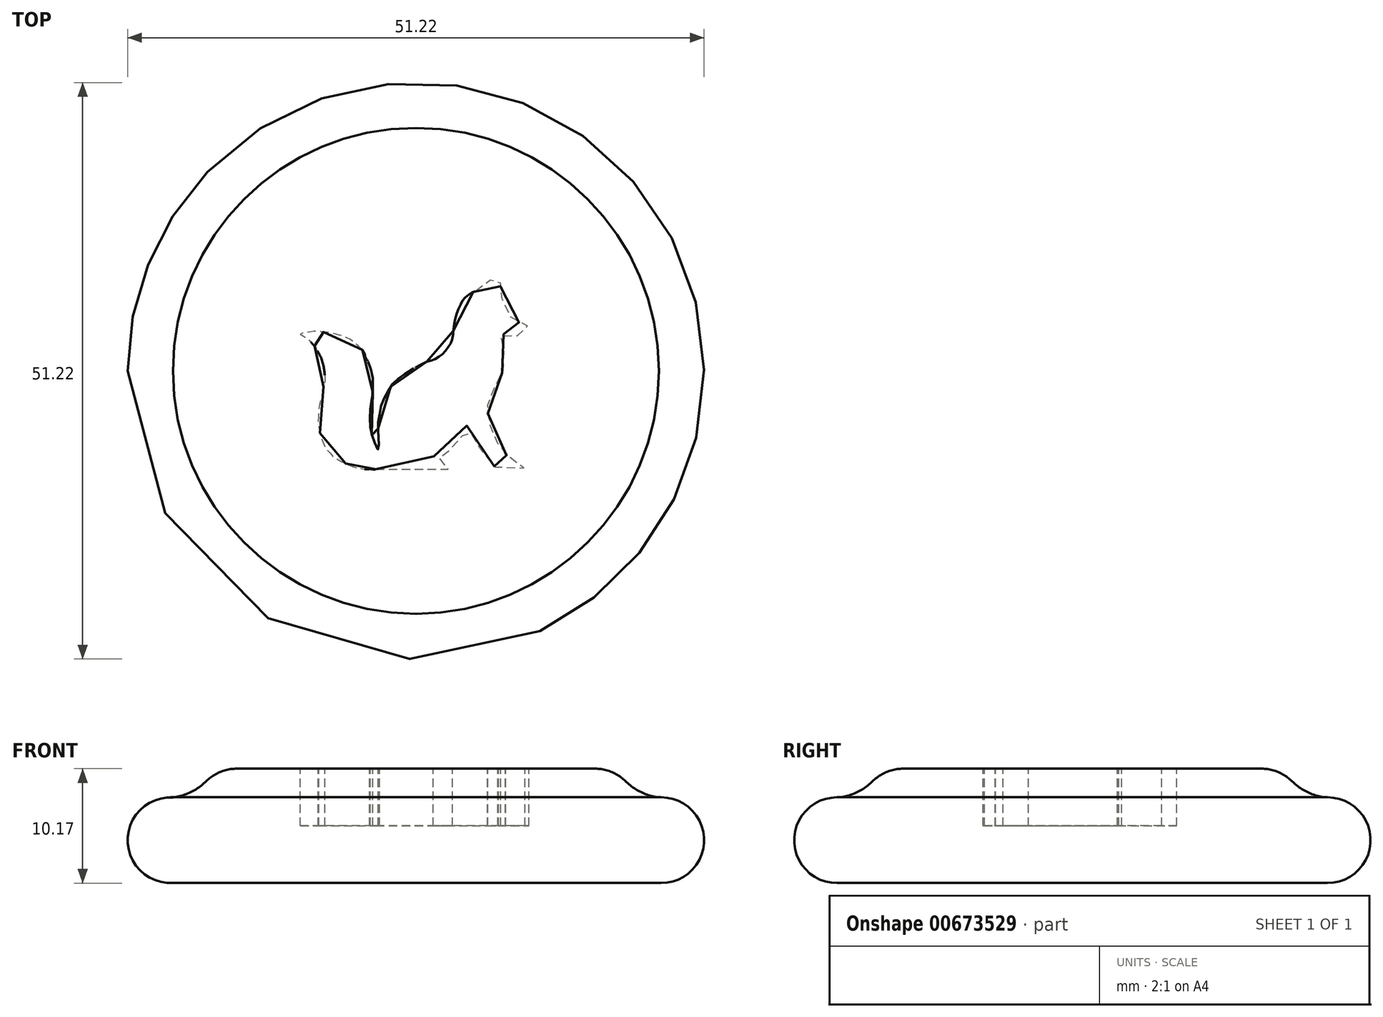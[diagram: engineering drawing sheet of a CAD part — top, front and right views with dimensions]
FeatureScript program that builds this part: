
annotation { "Feature Type Name" : "Feature", "Feature Type Description" : "" }
export const myFeature = defineFeature(function(context is Context, id is Id, definition is map)
    precondition{}
    {
        {
            var Q0;
            Q0=qCreatedBy(makeId("Front.planeOp"),FACE);
            var sketch = newSketch(context, id + "F0", { "sketchPlane" : qUnion([Q0])});
            skLineSegment(sketch, "E0", {"start": v(0, 0) * mm, "end": v(21.59, 0) * mm});
            skArc(sketch, "E1", {"start": v(0, 7.6) * mm, "mid": v(-4.02, 3.8) * mm, "end": v(0, 0) * mm});
            skLineSegment(sketch, "E2", {"start": v(21.59, 0) * mm, "end": v(21.59, 10.16) * mm});
            skPoint(sketch, "E3.visualSharp", {"position": v(3.81, 10.16) * mm});
            skLineSegment(sketch, "E4", {"start": v(5.65, 10.16) * mm, "end": v(21.59, 10.16) * mm});
            skArc(sketch, "E5", {"start": v(0, 7.6) * mm, "mid": v(1.6, 8.08) * mm, "end": v(2.97, 9.05) * mm});
            skArc(sketch, "E6.filletArc", {"start": v(5.65, 10.16) * mm, "mid": v(4.2, 9.87) * mm, "end": v(2.97, 9.05) * mm});
            skSolve(sketch);
        }
        {
            var Q0;
            Q0 = qSketchRegion(id + "F0", true);
            var Q1;
            Q1=sQuery(id+"F0.wireOp",EDGE,"E2");
            revolve(context, id + "F1", {"entities" : qUnion([Q0]), "axis" : qUnion([Q1]), "revolveType" : RevolveType.FULL});
        }
        {
            var Q0;
            Q0=makeQuery(id+"F1.opRevolve","SWEPT_FACE",FACE,{"disambiguationData":[OSD([sQuery(id+"F0.wireOp",EDGE,"E4")])]});
            var sketch = newSketch(context, id + "F2", { "sketchPlane" : qUnion([Q0])});
            skFitSpline(sketch, "E7", {"points": [v(18.03, -8.73) * mm, v(18.94, -8.7) * mm, v(24.12, -8.73) * mm, v(24.6, -8.7) * mm, v(24.84, -8.38) * mm, v(24.79, -8.15) * mm, v(24.6, -8.03) * mm, v(24.29, -7.88) * mm, v(23.99, -7.8) * mm, v(23.78, -7.76) * mm, v(23.48, -7.74) * mm, v(23.12, -7.65) * mm, v(23.43, -7.55) * mm, v(23.73, -7.48) * mm, v(23.96, -7.43) * mm, v(24.26, -7.26) * mm, v(24.5, -7.13) * mm, v(24.73, -6.96) * mm, v(24.93, -6.81) * mm, v(25.1, -6.72) * mm, v(25.26, -6.54) * mm, v(25.43, -6.35) * mm, v(25.57, -6.13) * mm, v(25.69, -5.83) * mm, v(25.82, -5.57) * mm, v(25.91, -5.3) * mm, v(26, -5.06) * mm, v(26.04, -4.78) * mm, v(26.15, -4.98) * mm, v(26.27, -5.28) * mm, v(26.42, -5.48) * mm, v(26.53, -5.61) * mm, v(26.62, -5.81) * mm, v(26.74, -6.02) * mm, v(26.87, -6.24) * mm, v(26.97, -6.46) * mm, v(27.16, -6.67) * mm, v(27.34, -6.93) * mm, v(27.44, -7.15) * mm, v(27.63, -7.37) * mm, v(27.82, -7.6) * mm, v(28.03, -7.83) * mm, v(28.22, -8.13) * mm, v(28.4, -8.31) * mm, v(28.53, -8.46) * mm, v(28.7, -8.6) * mm, v(28.84, -8.74) * mm, v(29.1, -8.76) * mm, v(29.25, -8.78) * mm, v(30.82, -8.81) * mm, v(30.99, -8.74) * mm, v(31.17, -8.65) * mm, v(31.25, -8.4) * mm, v(31.3, -8.22) * mm, v(31.26, -8) * mm, v(31.16, -7.83) * mm, v(30.92, -7.74) * mm, v(30.74, -7.72) * mm, v(29.97, -7.7) * mm, v(29.84, -7.57) * mm, v(29.7, -7.54) * mm, v(29.55, -7.43) * mm, v(29.35, -7.24) * mm, v(29.25, -7) * mm, v(29.13, -6.85) * mm, v(29.03, -6.68) * mm, v(28.9, -6.48) * mm, v(28.75, -6.2) * mm, v(28.63, -6) * mm, v(28.56, -5.81) * mm, v(28.5, -5.7) * mm, v(28.44, -5.57) * mm, v(28.37, -5.44) * mm, v(28.3, -5.15) * mm, v(28.19, -4.85) * mm, v(28.08, -4.57) * mm, v(28.02, -4.28) * mm, v(27.98, -4.02) * mm, v(27.98, -3.76) * mm, v(27.97, -3.54) * mm, v(27.97, -3.35) * mm, v(27.97, -3.1) * mm, v(27.98, -2.83) * mm, v(28, -2.67) * mm, v(28.08, -2.46) * mm, v(28.15, -2.28) * mm, v(28.22, -2.11) * mm, v(28.3, -2) * mm, v(28.39, -1.85) * mm, v(28.46, -1.67) * mm, v(28.6, -1.5) * mm, v(28.7, -1.26) * mm, v(28.77, -1.11) * mm, v(28.88, -0.85) * mm, v(29.03, -0.65) * mm, v(29.13, -0.45) * mm, v(29.2, -0.28) * mm, v(29.34, 0) * mm, v(29.47, 0.27) * mm, v(29.54, 0.46) * mm, v(29.55, 0.7) * mm, v(29.55, 0.89) * mm, v(29.55, 1.14) * mm, v(29.55, 1.46) * mm, v(29.5, 1.6) * mm, v(29.4, 1.77) * mm, v(29.34, 1.92) * mm, v(29.26, 2.09) * mm, v(29.16, 2.35) * mm, v(29.04, 2.51) * mm, v(28.95, 2.66) * mm, v(28.87, 2.8) * mm, v(28.92, 2.9) * mm, v(29.1, 3.03) * mm, v(29.22, 3.16) * mm, v(29.37, 3.24) * mm, v(29.58, 3.25) * mm, v(29.7, 3.24) * mm, v(29.9, 3.24) * mm, v(30.09, 3.22) * mm, v(30.28, 3.18) * mm, v(30.44, 3.12) * mm, v(30.59, 3.13) * mm, v(30.78, 3.13) * mm, v(30.91, 3.14) * mm, v(31.11, 3.23) * mm, v(31.27, 3.31) * mm, v(31.43, 3.4) * mm, v(31.54, 3.54) * mm, v(31.63, 3.67) * mm, v(31.58, 3.8) * mm, v(31.5, 4) * mm, v(31.34, 4.05) * mm, v(31.15, 4.15) * mm, v(30.95, 4.26) * mm, v(30.77, 4.3) * mm, v(30.56, 4.4) * mm, v(30.35, 4.54) * mm, v(30.14, 4.7) * mm, v(30, 4.81) * mm, v(29.85, 5.06) * mm, v(29.77, 5.27) * mm, v(29.73, 5.6) * mm, v(29.68, 5.86) * mm, v(29.57, 6.03) * mm, v(29.45, 6.23) * mm, v(29.24, 6.41) * mm, v(29.11, 6.5) * mm, v(29, 6.6) * mm, v(28.94, 6.65) * mm, v(29, 6.85) * mm, v(29.04, 7.05) * mm, v(29.05, 7.17) * mm, v(29.06, 7.34) * mm, v(29.12, 7.68) * mm, v(29.13, 7.8) * mm, v(29.13, 8) * mm, v(29.11, 8.23) * mm, v(29.06, 8.38) * mm, v(28.91, 8.39) * mm, v(28.72, 8.4) * mm, v(28.63, 8.34) * mm, v(28.5, 8.29) * mm, v(28.36, 8.2) * mm, v(28.16, 8.01) * mm, v(28.04, 7.88) * mm, v(27.77, 7.62) * mm, v(27.56, 7.48) * mm, v(27.41, 7.28) * mm, v(27.24, 7.12) * mm, v(27.18, 7.07) * mm, v(27.05, 7.06) * mm, v(26.88, 7.06) * mm, v(26.71, 7.01) * mm, v(26.6, 6.99) * mm, v(26.5, 6.92) * mm, v(26.38, 6.85) * mm, v(26.2, 6.7) * mm, v(26.04, 6.57) * mm, v(25.9, 6.42) * mm, v(25.79, 6.29) * mm, v(25.68, 6.14) * mm, v(25.6, 5.97) * mm, v(25.52, 5.83) * mm, v(25.42, 5.58) * mm, v(25.3, 5.35) * mm, v(25.2, 5.1) * mm, v(25.15, 4.85) * mm, v(25.08, 4.52) * mm, v(25.01, 4.24) * mm, v(24.97, 3.92) * mm, v(24.93, 3.65) * mm, v(24.9, 3.37) * mm, v(24.87, 3.15) * mm, v(24.8, 2.8) * mm, v(24.76, 2.6) * mm, v(24.67, 2.43) * mm, v(24.57, 2.26) * mm, v(24.48, 2.14) * mm, v(24.35, 1.92) * mm, v(24.23, 1.79) * mm, v(24.07, 1.6) * mm, v(23.89, 1.44) * mm, v(23.74, 1.3) * mm, v(23.57, 1.21) * mm, v(23.38, 1.08) * mm, v(23.25, 1.02) * mm, v(23.06, 0.93) * mm, v(22.87, 0.89) * mm, v(22.66, 0.85) * mm, v(22.5, 0.78) * mm, v(22.35, 0.7) * mm, v(22.17, 0.62) * mm, v(22.04, 0.56) * mm, v(21.9, 0.49) * mm, v(21.72, 0.4) * mm, v(21.51, 0.29) * mm, v(21.32, 0.15) * mm, v(20.8, -0.14) * mm, v(20.66, -0.25) * mm, v(20.53, -0.34) * mm, v(20.44, -0.43) * mm, v(20.27, -0.51) * mm, v(20.12, -0.62) * mm, v(20, -0.76) * mm, v(19.87, -0.9) * mm, v(19.71, -1.03) * mm, v(19.56, -1.15) * mm, v(19.43, -1.3) * mm, v(19.32, -1.48) * mm, v(19.2, -1.7) * mm, v(19.07, -1.86) * mm, v(19, -1.97) * mm, v(18.9, -2.18) * mm, v(18.79, -2.41) * mm, v(18.72, -2.63) * mm, v(18.66, -2.86) * mm, v(18.53, -3.02) * mm, v(18.5, -3.25) * mm, v(18.44, -3.56) * mm, v(18.4, -3.75) * mm, v(18.36, -3.96) * mm, v(18.31, -4.19) * mm, v(18.28, -4.36) * mm, v(18.27, -4.39) * mm, v(18.23, -4.68) * mm, v(18.23, -4.88) * mm, v(18.23, -5.05) * mm, v(18.24, -5.26) * mm, v(18.25, -5.34) * mm, v(18.28, -5.59) * mm, v(18.28, -5.74) * mm, v(18.27, -5.88) * mm, v(18.27, -6.1) * mm, v(18.28, -6.18) * mm, v(18.3, -6.32) * mm, v(18.3, -6.4) * mm, v(18.3, -6.63) * mm, v(18.3, -6.77) * mm, v(18.31, -6.89) * mm, v(18.36, -7.01) * mm, v(18.21, -7) * mm, v(18.1, -6.75) * mm, v(18.04, -6.63) * mm, v(17.97, -6.49) * mm, v(17.92, -6.34) * mm, v(17.87, -6.24) * mm, v(17.81, -6.03) * mm, v(17.74, -5.86) * mm, v(17.67, -5.7) * mm, v(17.64, -5.65) * mm, v(17.58, -5.39) * mm, v(17.55, -5.08) * mm, v(17.5, -4.83) * mm, v(17.53, -4.67) * mm, v(17.53, -4.45) * mm, v(17.49, -4.07) * mm, v(17.5, -3.84) * mm, v(17.5, -3.6) * mm, v(17.53, -3.38) * mm, v(17.56, -3.18) * mm, v(17.58, -3.13) * mm, v(17.6, -2.96) * mm, v(17.65, -2.69) * mm, v(17.66, -2.56) * mm, v(17.67, -2.46) * mm, v(17.7, -2.33) * mm, v(17.72, -2.14) * mm, v(17.74, -2.01) * mm, v(17.76, -1.84) * mm, v(17.77, -1.64) * mm, v(17.77, -1.43) * mm, v(17.77, -1.15) * mm, v(17.76, -0.86) * mm, v(17.75, -0.68) * mm, v(17.72, -0.4) * mm, v(17.7, -0.19) * mm, v(17.64, 0) * mm, v(17.56, 0.18) * mm, v(17.5, 0.3) * mm, v(17.4, 0.66) * mm, v(17.35, 0.84) * mm, v(17.3, 0.93) * mm, v(17.26, 0.98) * mm, v(17.1, 1.2) * mm, v(17.07, 1.44) * mm, v(16.96, 1.67) * mm, v(16.85, 1.84) * mm, v(16.76, 1.91) * mm, v(16.64, 2.02) * mm, v(16.5, 2.13) * mm, v(16.45, 2.25) * mm, v(16.32, 2.33) * mm, v(16.2, 2.43) * mm, v(16.04, 2.56) * mm, v(15.85, 2.7) * mm, v(15.62, 2.86) * mm, v(15.43, 2.94) * mm, v(15.22, 3.05) * mm, v(15, 3.1) * mm, v(14.77, 3.17) * mm, v(14.55, 3.24) * mm, v(14.35, 3.29) * mm, v(14.05, 3.35) * mm, v(13.78, 3.42) * mm, v(13.57, 3.44) * mm, v(13.33, 3.47) * mm, v(13.14, 3.49) * mm, v(12.89, 3.5) * mm, v(12.68, 3.5) * mm, v(12.54, 3.5) * mm, v(12.34, 3.47) * mm, v(12.01, 3.45) * mm, v(11.8, 3.4) * mm, v(11.6, 3.37) * mm, v(11.45, 3.34) * mm, v(11.31, 3.27) * mm, v(11.55, 3.12) * mm, v(11.69, 3.02) * mm, v(11.8, 2.94) * mm, v(11.92, 2.84) * mm, v(12.02, 2.78) * mm, v(12.15, 2.66) * mm, v(12.3, 2.53) * mm, v(12.42, 2.37) * mm, v(12.53, 2.27) * mm, v(12.68, 2.09) * mm, v(12.74, 1.9) * mm, v(12.78, 1.82) * mm, v(12.93, 1.62) * mm, v(13.03, 1.44) * mm, v(13.07, 1.33) * mm, v(13.13, 1.24) * mm, v(13.21, 1) * mm, v(13.25, 0.87) * mm, v(13.27, 0.8) * mm, v(13.35, 0.54) * mm, v(13.41, 0.26) * mm, v(13.45, 0) * mm, v(13.47, -0.2) * mm, v(13.5, -0.39) * mm, v(13.5, -0.67) * mm, v(13.5, -0.93) * mm, v(13.46, -1.13) * mm, v(13.41, -1.34) * mm, v(13.36, -1.5) * mm, v(13.34, -1.75) * mm, v(13.28, -2.03) * mm, v(13.21, -2.28) * mm, v(13.15, -2.5) * mm, v(13.1, -2.73) * mm, v(13.03, -3.06) * mm, v(13, -3.22) * mm, v(12.95, -3.55) * mm, v(12.96, -3.78) * mm, v(12.93, -4.06) * mm, v(12.91, -4.26) * mm, v(12.9, -4.49) * mm, v(12.92, -4.75) * mm, v(12.97, -4.9) * mm, v(12.98, -5.05) * mm, v(13.01, -5.31) * mm, v(13.07, -5.54) * mm, v(13.1, -5.76) * mm, v(13.19, -5.95) * mm, v(13.3, -6.19) * mm, v(13.41, -6.53) * mm, v(13.46, -6.7) * mm, v(13.53, -6.88) * mm, v(13.76, -7.1) * mm, v(13.88, -7.22) * mm, v(13.96, -7.29) * mm, v(14.03, -7.39) * mm, v(14.15, -7.52) * mm, v(14.26, -7.65) * mm, v(14.44, -7.8) * mm, v(14.64, -7.88) * mm, v(14.85, -8) * mm, v(14.9, -8.03) * mm, v(15.08, -8.11) * mm, v(15.22, -8.18) * mm, v(15.31, -8.23) * mm, v(15.36, -8.25) * mm, v(15.45, -8.28) * mm, v(15.58, -8.36) * mm, v(15.73, -8.42) * mm, v(15.8, -8.44) * mm, v(15.9, -8.48) * mm, v(15.96, -8.5) * mm, v(16.1, -8.56) * mm, v(16.17, -8.58) * mm, v(16.35, -8.64) * mm, v(16.5, -8.68) * mm, v(16.57, -8.69) * mm, v(16.68, -8.69) * mm, v(16.74, -8.7) * mm, v(16.87, -8.7) * mm, v(16.94, -8.72) * mm, v(17.02, -8.73) * mm, v(17.07, -8.74) * mm, v(17.19, -8.74) * mm, v(17.24, -8.74) * mm, v(17.32, -8.74) * mm, v(17.4, -8.74) * mm, v(17.51, -8.72) * mm, v(17.56, -8.73) * mm, v(17.67, -8.74) * mm, v(17.72, -8.75) * mm, v(17.89, -8.77) * mm, v(18.03, -8.73) * mm]});
            skSolve(sketch);
        }
        {
            var Q0;
            Q0 = qSketchRegion(id + "F2", true);
            extrude(context, id + "F3", {"entities" : qUnion([Q0]), "operationType" : NewBodyOperationType.REMOVE, "depth" : -5.08 * mm, "offsetDistance" : 25.4 * mm});
        }
    });
